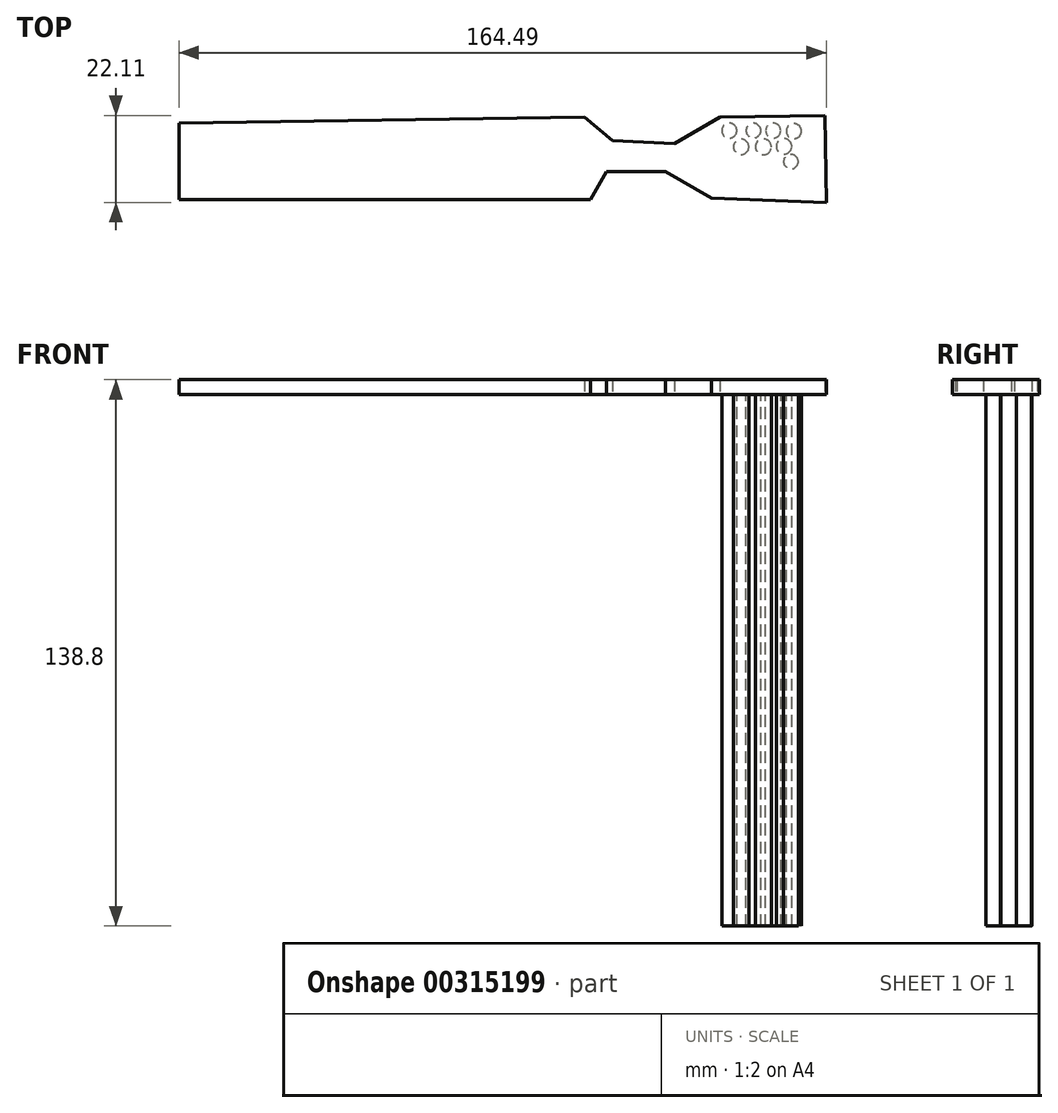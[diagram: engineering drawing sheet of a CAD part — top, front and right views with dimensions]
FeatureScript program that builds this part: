
annotation { "Feature Type Name" : "Feature", "Feature Type Description" : "" }
export const myFeature = defineFeature(function(context is Context, id is Id, definition is map)
    precondition{}
    {
        {
            var Q0;
            Q0=qCreatedBy(makeId("Top.planeOp"),FACE);
            var sketch = newSketch(context, id + "F0", { "sketchPlane" : qUnion([Q0])});
            skLineSegment(sketch, "E0", {"start": v(-94.26, 31.1) * mm, "end": v(-94.26, 11.24) * mm});
            skLineSegment(sketch, "E1", {"start": v(-94.26, 11.24) * mm, "end": v(10.28, 11.24) * mm});
            skLineSegment(sketch, "E2", {"start": v(10.28, 11.24) * mm, "end": v(14.4, 18.36) * mm});
            skLineSegment(sketch, "E3", {"start": v(14.4, 18.36) * mm, "end": v(29.4, 18.36) * mm});
            skLineSegment(sketch, "E4", {"start": v(29.4, 18.36) * mm, "end": v(41, 11.62) * mm});
            skLineSegment(sketch, "E5", {"start": v(41, 11.62) * mm, "end": v(70.23, 10.5) * mm});
            skLineSegment(sketch, "E6", {"start": v(70.23, 10.5) * mm, "end": v(69.86, 32.6) * mm});
            skLineSegment(sketch, "E7", {"start": v(69.86, 32.6) * mm, "end": v(43.24, 32.15) * mm});
            skLineSegment(sketch, "E8", {"start": v(43.24, 32.15) * mm, "end": v(31.64, 25.48) * mm});
            skLineSegment(sketch, "E9", {"start": v(31.64, 25.48) * mm, "end": v(15.9, 26.23) * mm});
            skLineSegment(sketch, "E10", {"start": v(15.9, 26.23) * mm, "end": v(8.78, 32.23) * mm});
            skLineSegment(sketch, "E11", {"start": v(8.78, 32.23) * mm, "end": v(-94.64, 30.73) * mm});
            skSolve(sketch);
        }
        {
            var Q0;
            {var subQ0=sQuery(id+"F0.wireOp",EDGE,"E1");Q0=makeQuery(id+"F0.imprint","IMPRINT",FACE,{"disambiguationData":[TD([[makeQuery(id+"F0.imprint","IMPRINT",EDGE,{"derivedFrom":subQ0}),1.0]])]});}
            extrude(context, id + "F1", {"entities" : qUnion([Q0]), "depth" : 3.82 * mm});
        }
        {
            var Q0;
            Q0=qCreatedBy(makeId("Top.planeOp"),FACE);
            var sketch = newSketch(context, id + "F2", { "sketchPlane" : qUnion([Q0])});
            skCircle(sketch, "E12", {"center": v(45.58, 28.77) * mm, "radius": 1.9 * mm});
            skCircle(sketch, "E13", {"center": v(51.72, 28.77) * mm, "radius": 1.88 * mm});
            skCircle(sketch, "E14", {"center": v(56.73, 28.77) * mm, "radius": 1.9 * mm});
            skCircle(sketch, "E15", {"center": v(61.99, 28.64) * mm, "radius": 1.92 * mm});
            skCircle(sketch, "E16", {"center": v(61.23, 20.88) * mm, "radius": 1.86 * mm});
            skCircle(sketch, "E17", {"center": v(59.48, 24.76) * mm, "radius": 1.96 * mm});
            skCircle(sketch, "E18", {"center": v(54.22, 24.63) * mm, "radius": 2.02 * mm});
            skCircle(sketch, "E19", {"center": v(48.59, 24.63) * mm, "radius": 1.96 * mm});
            skSolve(sketch);
        }
        {
            var Q0;
            Q0 = qSketchRegion(id + "F2", true);
            extrude(context, id + "F3", {"entities" : qUnion([Q0]), "operationType" : NewBodyOperationType.ADD, "oppositeDirection" : true, "depth" : 134.98 * mm});
        }
    });
